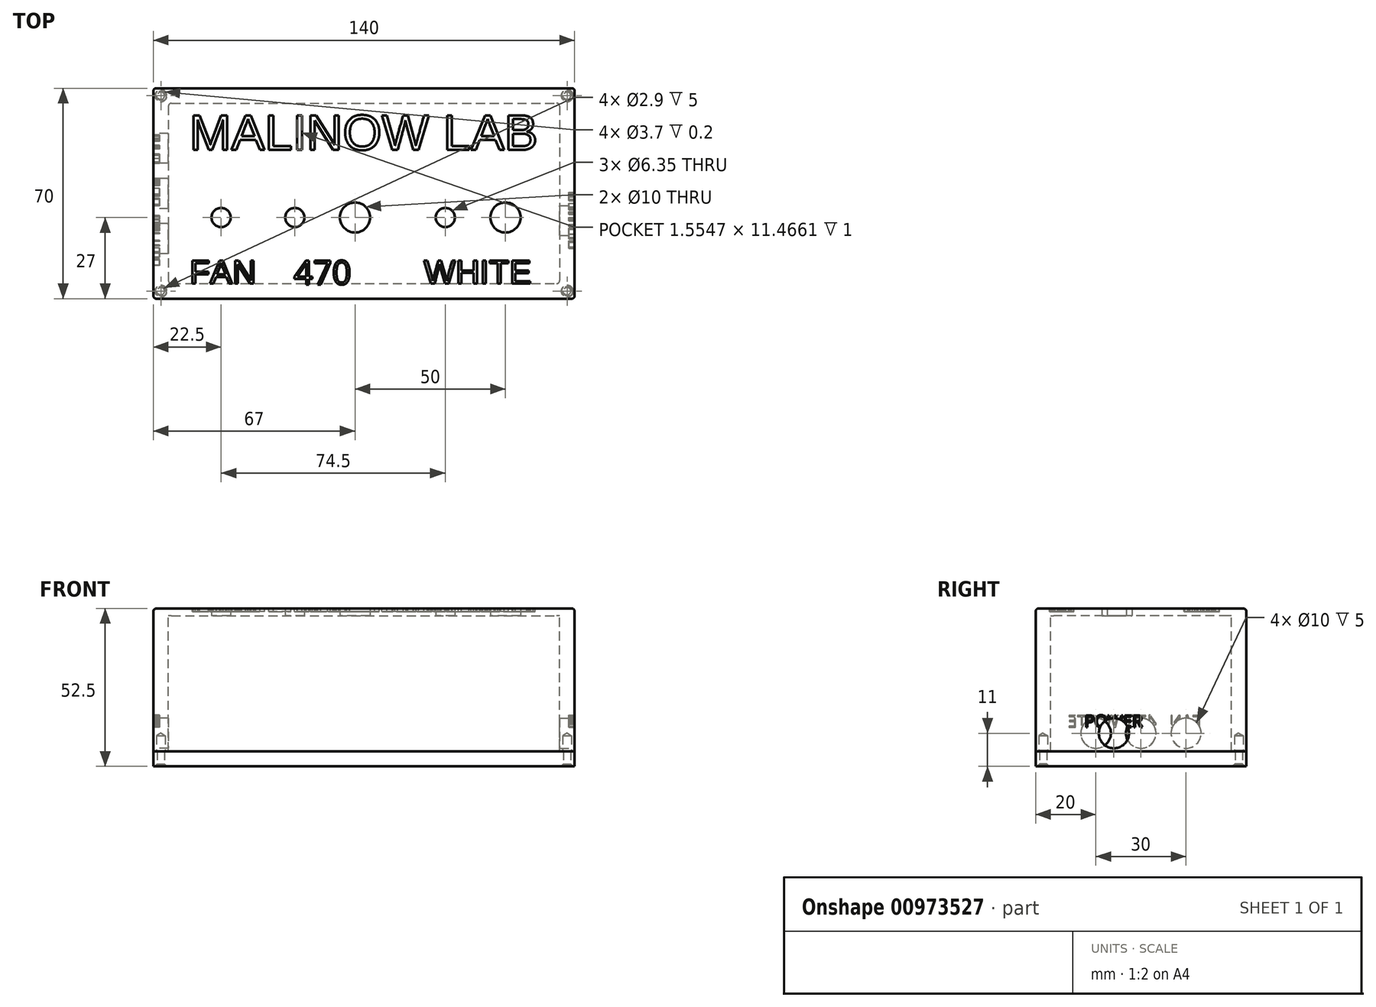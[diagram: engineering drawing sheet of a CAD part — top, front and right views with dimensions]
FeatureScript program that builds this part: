
annotation { "Feature Type Name" : "Feature", "Feature Type Description" : "" }
export const myFeature = defineFeature(function(context is Context, id is Id, definition is map)
    precondition{}
    {
        {
            var Q0;
            Q0=qCreatedBy(makeId("Top.planeOp"),FACE);
            var sketch = newSketch(context, id + "F0", { "sketchPlane" : qUnion([Q0])});
            skLineSegment(sketch, "E0.bottom", {"start": v(0, 0) * mm, "end": v(140, 0) * mm});
            skLineSegment(sketch, "E0.top", {"start": v(0, 70) * mm, "end": v(140, 70) * mm});
            skLineSegment(sketch, "E0.left", {"start": v(0, 0) * mm, "end": v(0, 70) * mm});
            skLineSegment(sketch, "E0.right", {"start": v(140, 0) * mm, "end": v(140, 70) * mm});
            skCircle(sketch, "E1", {"center": v(117, 27) * mm, "radius": 5 * mm});
            skCircle(sketch, "E2", {"center": v(67, 27) * mm, "radius": 5 * mm});
            skCircle(sketch, "E3", {"center": v(22.5, 27) * mm, "radius": 3.18 * mm});
            skLineSegment(sketch, "E4", {"start": v(5, 70) * mm, "end": v(5, 5) * mm, "construction": true});
            skLineSegment(sketch, "E5", {"start": v(5, 5) * mm, "end": v(135, 5) * mm, "construction": true});
            skLineSegment(sketch, "E6", {"start": v(135, 5) * mm, "end": v(135, 70) * mm, "construction": true});
            skLineSegment(sketch, "E7", {"start": v(0, 65) * mm, "end": v(140, 65) * mm, "construction": true});
            skLineSegment(sketch, "E8", {"start": v(5, 5) * mm, "end": v(0, 5) * mm, "construction": true});
            skLineSegment(sketch, "E9", {"start": v(135, 5) * mm, "end": v(140, 5) * mm, "construction": true});
            skPoint(sketch, "E10.endSnap0", {"position": v(5, 37.5) * mm});
            skLineSegment(sketch, "E11", {"start": v(5, 70) * mm, "end": v(135, 65) * mm, "construction": true});
            skLineSegment(sketch, "E12", {"start": v(135, 70) * mm, "end": v(5, 65) * mm, "construction": true});
            skLineSegment(sketch, "E13", {"start": v(140, 5) * mm, "end": v(0, 0) * mm, "construction": true});
            skLineSegment(sketch, "E14", {"start": v(0, 5) * mm, "end": v(140, 0) * mm, "construction": true});
            skPoint(sketch, "E15", {"position": v(70, 2.5) * mm});
            skPoint(sketch, "E16", {"position": v(70, 67.5) * mm});
            skLineSegment(sketch, "E17", {"start": v(5, 27) * mm, "end": v(135, 27) * mm, "construction": true});
            skCircle(sketch, "E18", {"center": v(47, 27) * mm, "radius": 3.18 * mm});
            skCircle(sketch, "E19", {"center": v(97, 27) * mm, "radius": 3.18 * mm});
            skSolve(sketch);
        }
        {
            var Q0;
            Q0=makeQuery(id+"F0.imprint","IMPRINT",FACE,{"disambiguationData":[TD([[makeQuery(id+"F0.imprint","IMPRINT",EDGE,{"derivedFrom":sQuery(id+"F0.wireOp",EDGE,"E0.bottom")}),1.0]])]});
            extrude(context, id + "F1", {"entities" : qUnion([Q0]), "depth" : 2.5 * mm, "offsetDistance" : 25 * mm});
        }
        {
            var Q0;
            Q0=makeQuery(id+"F1.opExtrude","CAP_FACE",FACE,{"disambiguationData":[OSD([sQuery(id+"F0.wireOp",EDGE,"E0.bottom"),sQuery(id+"F0.wireOp",EDGE,"E0.top"),sQuery(id+"F0.wireOp",EDGE,"E0.left"),sQuery(id+"F0.wireOp",EDGE,"E0.right"),sQuery(id+"F0.wireOp",EDGE,"E1"),sQuery(id+"F0.wireOp",EDGE,"E2"),sQuery(id+"F0.wireOp",EDGE,"E3")])],"isStart":true});
            var sketch = newSketch(context, id + "F2", { "sketchPlane" : qUnion([Q0])});
            skLineSegment(sketch, "E20.bottom", {"start": v(0, -70) * mm, "end": v(140, -70) * mm, "construction": true});
            skLineSegment(sketch, "E20.top", {"start": v(0, 0) * mm, "end": v(140, 0) * mm, "construction": true});
            skLineSegment(sketch, "E20.left", {"start": v(0, -70) * mm, "end": v(0, 0) * mm, "construction": true});
            skLineSegment(sketch, "E20.right", {"start": v(140, -70) * mm, "end": v(140, 0) * mm, "construction": true});
            skLineSegment(sketch, "E21.bottom", {"start": v(5, -65) * mm, "end": v(135, -65) * mm});
            skLineSegment(sketch, "E21.top", {"start": v(5, -5) * mm, "end": v(135, -5) * mm});
            skLineSegment(sketch, "E21.left", {"start": v(5, -65) * mm, "end": v(5, -5) * mm});
            skLineSegment(sketch, "E21.right", {"start": v(135, -65) * mm, "end": v(135, -5) * mm});
            skSolve(sketch);
        }
        {
            var Q0;
            Q0=makeQuery(id+"F2.imprint","IMPRINT",FACE,{"disambiguationData":[TD([[makeQuery(id+"F2.imprint","IMPRINT",EDGE,{"derivedFrom":sQuery(id+"F2.wireOp",EDGE,"E21.bottom")}),-1.0]])]});
            var Q1;
            Q1=makeQuery(id+"F2.imprint","IMPRINT",FACE,{"disambiguationData":[TD([[makeQuery(id+"F2.imprint","IMPRINT",EDGE,{"derivedFrom":makeQuery(id+"FxvTJw6m9mzOm3c_1.hole-0.boolean.opBoolean","INTERSECT",EDGE,{"derivedFrom":[makeQuery(id+"F1.opExtrude","CAP_FACE",FACE,{"disambiguationData":[OSD([sQuery(id+"F0.wireOp",EDGE,"E0.bottom"),sQuery(id+"F0.wireOp",EDGE,"E0.top"),sQuery(id+"F0.wireOp",EDGE,"E0.left"),sQuery(id+"F0.wireOp",EDGE,"E0.right"),sQuery(id+"F0.wireOp",EDGE,"E1"),sQuery(id+"F0.wireOp",EDGE,"E2"),sQuery(id+"F0.wireOp",EDGE,"E3")])],"isStart":true}),makeQuery(id+"FxvTJw6m9mzOm3c_1.hole-0.opRevolve","SWEPT_FACE",FACE,{"disambiguationData":[OSD([sQuery(id+"FxvTJw6m9mzOm3c_1.hole-0.sketch.wireOp",EDGE,"core_line_2")])]})]})}),1.0]])]});
            var Q2;
            Q2=makeQuery(id+"F2.imprint","IMPRINT",FACE,{"disambiguationData":[TD([[makeQuery(id+"F2.imprint","IMPRINT",EDGE,{"derivedFrom":makeQuery(id+"FxvTJw6m9mzOm3c_1.hole-1.boolean.opBoolean","INTERSECT",EDGE,{"derivedFrom":[makeQuery(id+"F1.opExtrude","CAP_FACE",FACE,{"disambiguationData":[OSD([sQuery(id+"F0.wireOp",EDGE,"E0.bottom"),sQuery(id+"F0.wireOp",EDGE,"E0.top"),sQuery(id+"F0.wireOp",EDGE,"E0.left"),sQuery(id+"F0.wireOp",EDGE,"E0.right"),sQuery(id+"F0.wireOp",EDGE,"E1"),sQuery(id+"F0.wireOp",EDGE,"E2"),sQuery(id+"F0.wireOp",EDGE,"E3")])],"isStart":true}),makeQuery(id+"FxvTJw6m9mzOm3c_1.hole-1.opRevolve","SWEPT_FACE",FACE,{"disambiguationData":[OSD([sQuery(id+"FxvTJw6m9mzOm3c_1.hole-1.sketch.wireOp",EDGE,"core_line_2")])]})]})}),1.0]])]});
            var Q3;
            Q3=makeQuery(id+"F2.imprint","IMPRINT",FACE,{"disambiguationData":[TD([[makeQuery(id+"F2.imprint","IMPRINT",EDGE,{"derivedFrom":makeQuery(id+"FxvTJw6m9mzOm3c_1.hole-2.boolean.opBoolean","INTERSECT",EDGE,{"derivedFrom":[makeQuery(id+"F1.opExtrude","CAP_FACE",FACE,{"disambiguationData":[OSD([sQuery(id+"F0.wireOp",EDGE,"E0.bottom"),sQuery(id+"F0.wireOp",EDGE,"E0.top"),sQuery(id+"F0.wireOp",EDGE,"E0.left"),sQuery(id+"F0.wireOp",EDGE,"E0.right"),sQuery(id+"F0.wireOp",EDGE,"E1"),sQuery(id+"F0.wireOp",EDGE,"E2"),sQuery(id+"F0.wireOp",EDGE,"E3")])],"isStart":true}),makeQuery(id+"FxvTJw6m9mzOm3c_1.hole-2.opRevolve","SWEPT_FACE",FACE,{"disambiguationData":[OSD([sQuery(id+"FxvTJw6m9mzOm3c_1.hole-2.sketch.wireOp",EDGE,"core_line_2")])]})]})}),1.0]])]});
            var Q4;
            Q4=makeQuery(id+"F2.imprint","IMPRINT",FACE,{"disambiguationData":[TD([[makeQuery(id+"F2.imprint","IMPRINT",EDGE,{"derivedFrom":makeQuery(id+"FxvTJw6m9mzOm3c_1.hole-3.boolean.opBoolean","INTERSECT",EDGE,{"derivedFrom":[makeQuery(id+"F1.opExtrude","CAP_FACE",FACE,{"disambiguationData":[OSD([sQuery(id+"F0.wireOp",EDGE,"E0.bottom"),sQuery(id+"F0.wireOp",EDGE,"E0.top"),sQuery(id+"F0.wireOp",EDGE,"E0.left"),sQuery(id+"F0.wireOp",EDGE,"E0.right"),sQuery(id+"F0.wireOp",EDGE,"E1"),sQuery(id+"F0.wireOp",EDGE,"E2"),sQuery(id+"F0.wireOp",EDGE,"E3")])],"isStart":true}),makeQuery(id+"FxvTJw6m9mzOm3c_1.hole-3.opRevolve","SWEPT_FACE",FACE,{"disambiguationData":[OSD([sQuery(id+"FxvTJw6m9mzOm3c_1.hole-3.sketch.wireOp",EDGE,"core_line_2")])]})]})}),1.0]])]});
            extrude(context, id + "F3", {"entities" : qUnion([Q0, Q1, Q2, Q3, Q4]), "depth" : 45 * mm, "offsetDistance" : 25 * mm});
        }
        {
            var Q0;
            Q0=makeQuery(id+"F3.opExtrude","CAP_FACE",FACE,{"disambiguationData":[OSD([sQuery(id+"F0.wireOp",EDGE,"E0.bottom"),sQuery(id+"F0.wireOp",EDGE,"E0.top"),sQuery(id+"F0.wireOp",EDGE,"E0.left"),sQuery(id+"F0.wireOp",EDGE,"E0.right"),sQuery(id+"F2.wireOp",EDGE,"E21.bottom"),sQuery(id+"F2.wireOp",EDGE,"E21.top"),sQuery(id+"F2.wireOp",EDGE,"E21.left"),sQuery(id+"F2.wireOp",EDGE,"E21.right")])],"isStart":false});
            var sketch = newSketch(context, id + "F4", { "sketchPlane" : qUnion([Q0])});
            skLineSegment(sketch, "E22.bottom", {"start": v(0, 0) * mm, "end": v(140, 0) * mm});
            skLineSegment(sketch, "E22.top", {"start": v(0, -70) * mm, "end": v(140, -70) * mm});
            skLineSegment(sketch, "E22.left", {"start": v(0, 0) * mm, "end": v(0, -70) * mm});
            skLineSegment(sketch, "E22.right", {"start": v(140, 0) * mm, "end": v(140, -70) * mm});
            skLineSegment(sketch, "E23.bottom", {"start": v(5, -5) * mm, "end": v(135, -5) * mm, "construction": true});
            skLineSegment(sketch, "E23.top", {"start": v(5, -65) * mm, "end": v(135, -65) * mm, "construction": true});
            skLineSegment(sketch, "E23.left", {"start": v(5, -5) * mm, "end": v(5, -65) * mm, "construction": true});
            skLineSegment(sketch, "E23.right", {"start": v(135, -5) * mm, "end": v(135, -65) * mm, "construction": true});
            skSolve(sketch);
        }
        {
            var Q0;
            Q0=makeQuery(id+"F4.imprint","IMPRINT",FACE,{"disambiguationData":[TD([[makeQuery(id+"F4.imprint","IMPRINT",EDGE,{"derivedFrom":sQuery(id+"F4.wireOp",EDGE,"E22.bottom")}),-1.0]])]});
            var Q1;
            Q1=makeQuery(id+"F4.imprint","IMPRINT",FACE,{"disambiguationData":[TD([[makeQuery(id+"F4.imprint","IMPRINT",EDGE,{"derivedFrom":makeQuery(id+"F3.opExtrude","CAP_EDGE",EDGE,{"disambiguationData":[OSD([sQuery(id+"F2.wireOp",EDGE,"E21.bottom")])],"isStart":false})}),1.0]])]});
            extrude(context, id + "F5", {"entities" : qUnion([Q0, Q1]), "depth" : 5 * mm, "offsetDistance" : 25 * mm});
        }
        {
            var Q0;
            Q0=makeQuery(id+"F5.opExtrude","CAP_FACE",FACE,{"disambiguationData":[OSD([sQuery(id+"F4.wireOp",EDGE,"E22.bottom"),sQuery(id+"F4.wireOp",EDGE,"E22.top"),sQuery(id+"F4.wireOp",EDGE,"E22.left"),sQuery(id+"F4.wireOp",EDGE,"E22.right")])],"isStart":false});
            var sketch = newSketch(context, id + "F6", { "sketchPlane" : qUnion([Q0])});
            skLineSegment(sketch, "E24.bottom", {"start": v(0, -70) * mm, "end": v(140, -70) * mm, "construction": true});
            skLineSegment(sketch, "E24.top", {"start": v(0, 0) * mm, "end": v(140, 0) * mm, "construction": true});
            skLineSegment(sketch, "E24.left", {"start": v(0, -70) * mm, "end": v(0, 0) * mm, "construction": true});
            skLineSegment(sketch, "E24.right", {"start": v(140, -70) * mm, "end": v(140, 0) * mm, "construction": true});
            skLineSegment(sketch, "E25.bottom", {"start": v(5, -65) * mm, "end": v(135, -65) * mm, "construction": true});
            skLineSegment(sketch, "E25.top", {"start": v(5, -5) * mm, "end": v(135, -5) * mm, "construction": true});
            skLineSegment(sketch, "E25.left", {"start": v(5, -65) * mm, "end": v(5, -5) * mm, "construction": true});
            skLineSegment(sketch, "E25.right", {"start": v(135, -65) * mm, "end": v(135, -5) * mm, "construction": true});
            skLineSegment(sketch, "E26", {"start": v(5, -5) * mm, "end": v(0, 0) * mm, "construction": true});
            skLineSegment(sketch, "E27", {"start": v(135, -5) * mm, "end": v(140, 0) * mm, "construction": true});
            skLineSegment(sketch, "E28", {"start": v(135, -65) * mm, "end": v(140, -70) * mm, "construction": true});
            skLineSegment(sketch, "E29", {"start": v(5, -65) * mm, "end": v(0, -70) * mm, "construction": true});
            skPoint(sketch, "E30", {"position": v(2.5, -2.5) * mm});
            skPoint(sketch, "E31", {"position": v(137.5, -2.5) * mm});
            skPoint(sketch, "E32", {"position": v(137.5, -67.5) * mm});
            skPoint(sketch, "E33", {"position": v(2.5, -67.5) * mm});
            skSolve(sketch);
        }
        {
            var Q0;
            Q0=sQuery(id+"F6.wireOp",VERTEX,"E30");
            var Q1;
            Q1=sQuery(id+"F6.wireOp",VERTEX,"E33");
            var Q2;
            Q2=sQuery(id+"F6.wireOp",VERTEX,"E32");
            var Q3;
            Q3=sQuery(id+"F6.wireOp",VERTEX,"E31");
            var Q4;
            Q4=makeQuery(id+"F3.opExtrude","SWEPT_BODY",BODY,{"disambiguationData":[OSD([sQuery(id+"F0.wireOp",EDGE,"E0.bottom"),sQuery(id+"F0.wireOp",EDGE,"E0.top"),sQuery(id+"F0.wireOp",EDGE,"E0.left"),sQuery(id+"F0.wireOp",EDGE,"E0.right"),sQuery(id+"F2.wireOp",EDGE,"E21.bottom"),sQuery(id+"F2.wireOp",EDGE,"E21.top"),sQuery(id+"F2.wireOp",EDGE,"E21.left"),sQuery(id+"F2.wireOp",EDGE,"E21.right")])]});
            var Q5;
            Q5=makeQuery(id+"F5.opExtrude","SWEPT_BODY",BODY,{"disambiguationData":[OSD([sQuery(id+"F4.wireOp",EDGE,"E22.bottom"),sQuery(id+"F4.wireOp",EDGE,"E22.top"),sQuery(id+"F4.wireOp",EDGE,"E22.left"),sQuery(id+"F4.wireOp",EDGE,"E22.right")])]});
            hole(context, id + "F7", {"style" : HoleStyle.C_SINK, "endStyle" : HoleEndStyle.BLIND, "holeDiameter" : 2.4 * mm, "cSinkDiameter" : 4 * mm, "cSinkAngle" : 90 * degree, "majorDiameter" : 5 * mm, "holeDepth" : 5 * mm, "isTappedThrough" : true, "tappedDepth" : 12 * mm, "tapClearance" : 3, "locations" : qUnion([Q0, Q1, Q2, Q3]), "scope" : qUnion([Q4, Q5])});
        }
        {
            var Q0;
            Q0=makeQuery(id+"F3.opExtrude","CAP_FACE",FACE,{"disambiguationData":[OSD([sQuery(id+"F0.wireOp",EDGE,"E0.bottom"),sQuery(id+"F0.wireOp",EDGE,"E0.top"),sQuery(id+"F0.wireOp",EDGE,"E0.left"),sQuery(id+"F0.wireOp",EDGE,"E0.right"),sQuery(id+"F2.wireOp",EDGE,"E21.bottom"),sQuery(id+"F2.wireOp",EDGE,"E21.top"),sQuery(id+"F2.wireOp",EDGE,"E21.left"),sQuery(id+"F2.wireOp",EDGE,"E21.right")])],"isStart":false});
            var sketch = newSketch(context, id + "F8", { "sketchPlane" : qUnion([Q0])});
            skPoint(sketch, "E34", {"position": v(2.5, -2.5) * mm});
            skPoint(sketch, "E35", {"position": v(2.5, -67.5) * mm});
            skPoint(sketch, "E36", {"position": v(137.5, -67.5) * mm});
            skPoint(sketch, "E37", {"position": v(137.5, -2.5) * mm});
            skSolve(sketch);
        }
        {
            var Q0;
            Q0=sQuery(id+"F8.wireOp",VERTEX,"E34");
            var Q1;
            Q1=sQuery(id+"F8.wireOp",VERTEX,"E35");
            var Q2;
            Q2=sQuery(id+"F8.wireOp",VERTEX,"E36");
            var Q3;
            Q3=sQuery(id+"F8.wireOp",VERTEX,"E37");
            var Q4;
            Q4=makeQuery(id+"F3.opExtrude","SWEPT_BODY",BODY,{"disambiguationData":[OSD([sQuery(id+"F0.wireOp",EDGE,"E0.bottom"),sQuery(id+"F0.wireOp",EDGE,"E0.top"),sQuery(id+"F0.wireOp",EDGE,"E0.left"),sQuery(id+"F0.wireOp",EDGE,"E0.right"),sQuery(id+"F2.wireOp",EDGE,"E21.bottom"),sQuery(id+"F2.wireOp",EDGE,"E21.top"),sQuery(id+"F2.wireOp",EDGE,"E21.left"),sQuery(id+"F2.wireOp",EDGE,"E21.right")])]});
            hole(context, id + "F9", {"style" : HoleStyle.C_BORE, "endStyle" : HoleEndStyle.BLIND, "holeDiameter" : 2.9 * mm, "cBoreDiameter" : 3.7 * mm, "cBoreDepth" : .2 * mm, "majorDiameter" : 5 * mm, "holeDepth" : 5.2 * mm, "isTappedThrough" : true, "tappedDepth" : 12 * mm, "tapClearance" : 3, "locations" : qUnion([Q0, Q1, Q2, Q3]), "scope" : qUnion([Q4])});
        }
        {
            var Q0;
            Q0=makeQuery(id+"F1.opExtrude","CAP_EDGE",EDGE,{"disambiguationData":[OSD([sQuery(id+"F0.wireOp",EDGE,"E0.bottom")])],"isStart":false});
            var Q1;
            Q1=makeQuery(id+"F1.opExtrude","CAP_EDGE",EDGE,{"disambiguationData":[OSD([sQuery(id+"F0.wireOp",EDGE,"E0.left")])],"isStart":false});
            var Q2;
            Q2=makeQuery(id+"F1.opExtrude","CAP_EDGE",EDGE,{"disambiguationData":[OSD([sQuery(id+"F0.wireOp",EDGE,"E0.top")])],"isStart":false});
            var Q3;
            Q3=makeQuery(id+"F1.opExtrude","CAP_EDGE",EDGE,{"disambiguationData":[OSD([sQuery(id+"F0.wireOp",EDGE,"E0.right")])],"isStart":false});
            var Q4;
            Q4=makeQuery(id+"F3.opExtrude","SWEPT_EDGE",EDGE,{"disambiguationData":[OSD([sQuery(id+"F0.wireOp",EDGE,"E0.bottom"),sQuery(id+"F0.wireOp",EDGE,"E0.right")])]});
            var Q5;
            Q5=makeQuery(id+"F3.opExtrude","SWEPT_EDGE",EDGE,{"disambiguationData":[OSD([sQuery(id+"F0.wireOp",EDGE,"E0.bottom"),sQuery(id+"F0.wireOp",EDGE,"E0.left")])]});
            var Q6;
            Q6=makeQuery(id+"F1.opExtrude","SWEPT_EDGE",EDGE,{"disambiguationData":[OSD([sQuery(id+"F0.wireOp",EDGE,"E0.bottom"),sQuery(id+"F0.wireOp",EDGE,"E0.left")])]});
            var Q7;
            Q7=makeQuery(id+"F1.opExtrude","SWEPT_EDGE",EDGE,{"disambiguationData":[OSD([sQuery(id+"F0.wireOp",EDGE,"E0.bottom"),sQuery(id+"F0.wireOp",EDGE,"E0.right")])]});
            var Q8;
            Q8=makeQuery(id+"F3.opExtrude","SWEPT_EDGE",EDGE,{"disambiguationData":[OSD([sQuery(id+"F0.wireOp",EDGE,"E0.top"),sQuery(id+"F0.wireOp",EDGE,"E0.right")])]});
            var Q9;
            Q9=makeQuery(id+"F1.opExtrude","SWEPT_EDGE",EDGE,{"disambiguationData":[OSD([sQuery(id+"F0.wireOp",EDGE,"E0.top"),sQuery(id+"F0.wireOp",EDGE,"E0.right")])]});
            var Q10;
            Q10=makeQuery(id+"F3.opExtrude","SWEPT_EDGE",EDGE,{"disambiguationData":[OSD([sQuery(id+"F0.wireOp",EDGE,"E0.top"),sQuery(id+"F0.wireOp",EDGE,"E0.left")])]});
            var Q11;
            Q11=makeQuery(id+"F1.opExtrude","SWEPT_EDGE",EDGE,{"disambiguationData":[OSD([sQuery(id+"F0.wireOp",EDGE,"E0.top"),sQuery(id+"F0.wireOp",EDGE,"E0.left")])]});
            var Q12;
            Q12=makeQuery(id+"F5.opExtrude","SWEPT_EDGE",EDGE,{"disambiguationData":[OSD([sQuery(id+"F4.wireOp",EDGE,"E22.top"),sQuery(id+"F4.wireOp",EDGE,"E22.left")])]});
            var Q13;
            Q13=makeQuery(id+"F5.opExtrude","SWEPT_EDGE",EDGE,{"disambiguationData":[OSD([sQuery(id+"F4.wireOp",EDGE,"E22.bottom"),sQuery(id+"F4.wireOp",EDGE,"E22.left")])]});
            var Q14;
            Q14=makeQuery(id+"F5.opExtrude","SWEPT_EDGE",EDGE,{"disambiguationData":[OSD([sQuery(id+"F4.wireOp",EDGE,"E22.top"),sQuery(id+"F4.wireOp",EDGE,"E22.right")])]});
            var Q15;
            Q15=makeQuery(id+"F5.opExtrude","SWEPT_EDGE",EDGE,{"disambiguationData":[OSD([sQuery(id+"F4.wireOp",EDGE,"E22.bottom"),sQuery(id+"F4.wireOp",EDGE,"E22.right")])]});
            fillet(context, id + "F10", {"entities" : qUnion([Q0, Q1, Q2, Q3, Q4, Q5, Q6, Q7, Q8, Q9, Q10, Q11, Q12, Q13, Q14, Q15]), "radius" : 1 * mm, "tangentPropagation" : true, "allowEdgeOverflow" : false});
        }
        {
            var Q0;
            Q0=makeQuery(id+"F3.opExtrude","SWEPT_FACE",FACE,{"disambiguationData":[OSD([sQuery(id+"F0.wireOp",EDGE,"E0.left")])]});
            var sketch = newSketch(context, id + "F11", { "sketchPlane" : qUnion([Q0])});
            skCircle(sketch, "E38", {"center": v(-20, -39) * mm, "radius": 5 * mm});
            skLineSegment(sketch, "E39", {"start": v(-35, -45) * mm, "end": v(-35, 0) * mm, "construction": true});
            skLineSegment(sketch, "E40", {"start": v(-20, -39) * mm, "end": v(-70.23, -39) * mm, "construction": true});
            skCircle(sketch, "E41", {"center": v(-35, -39) * mm, "radius": 5 * mm});
            skCircle(sketch, "E42", {"center": v(-50, -39) * mm, "radius": 5 * mm});
            skSolve(sketch);
        }
        {
            var Q0;
            Q0=makeQuery(id+"F3.opExtrude","SWEPT_FACE",FACE,{"disambiguationData":[OSD([sQuery(id+"F0.wireOp",EDGE,"E0.right")])]});
            var sketch = newSketch(context, id + "F12", { "sketchPlane" : qUnion([Q0])});
            skLineSegment(sketch, "E43", {"start": v(1, -39) * mm, "end": v(69, -39) * mm, "construction": true});
            skCircle(sketch, "E44", {"center": v(26, -39) * mm, "radius": 5 * mm});
            skCircle(sketch, "E45", {"center": v(40, -39) * mm, "radius": 5 * mm});
            skCircle(sketch, "E46", {"center": v(54, -39) * mm, "radius": 5 * mm});
            skSolve(sketch);
        }
        {
            var Q0;
            Q0=makeQuery(id+"F10.opFillet","SPLIT",FACE,{"disambiguationData":[OD(4.0)],"derivedFrom":makeQuery(id+"F1.opExtrude","CAP_FACE",FACE,{"disambiguationData":[OSD([sQuery(id+"F0.wireOp",EDGE,"E0.bottom"),sQuery(id+"F0.wireOp",EDGE,"E0.top"),sQuery(id+"F0.wireOp",EDGE,"E0.left"),sQuery(id+"F0.wireOp",EDGE,"E0.right"),sQuery(id+"F0.wireOp",EDGE,"E1"),sQuery(id+"F0.wireOp",EDGE,"E2"),sQuery(id+"F0.wireOp",EDGE,"E3")])],"isStart":false})});
            var sketch = newSketch(context, id + "F13", { "sketchPlane" : qUnion([Q0])});
            skLineSegment(sketch, "E47.bottom", {"start": v(1, 61.5) * mm, "end": v(139, 61.5) * mm, "construction": true});
            skLineSegment(sketch, "E47.top", {"start": v(1, 49.5) * mm, "end": v(139, 49.5) * mm, "construction": true});
            skLineSegment(sketch, "E47.left", {"start": v(1, 61.5) * mm, "end": v(1, 49.5) * mm, "construction": true});
            skLineSegment(sketch, "E47.right", {"start": v(139, 61.5) * mm, "end": v(139, 49.5) * mm, "construction": true});
            skLineSegment(sketch, "E48", {"start": v(70, 61.5) * mm, "end": v(70, 49.5) * mm, "construction": true});
            skLineSegment(sketch, "E49.bottom", {"start": v(100.24, 61.5) * mm, "end": v(11.98, 61.5) * mm, "construction": true});
            skLineSegment(sketch, "E49.top", {"start": v(128.02, 49.5) * mm, "end": v(39.76, 49.5) * mm, "construction": true});
            skLineSegment(sketch, "E49.left", {"start": v(100.24, 61.5) * mm, "end": v(128.02, 49.5) * mm, "construction": true});
            skLineSegment(sketch, "E49.right", {"start": v(11.98, 61.5) * mm, "end": v(39.76, 49.5) * mm, "construction": true});
            skPoint(sketch, "E49.middle", {"position": v(70, 55.5) * mm});
            skText(sketch, "E50", { "text": "MALINOW LAB", "fontName": "Arimo-Regular.ttf"});
            const initialGuessF13  = {"E50": [0.01198, 0.0495, 1, 0, 0.012]};
            skSetInitialGuess(sketch, initialGuessF13);
            skSolve(sketch);
        }
        {
            var Q0;
            Q0=qSketchRegion(id+"F13",true);
            extrude(context, id + "F14", {"entities" : qUnion([Q0]), "operationType" : NewBodyOperationType.REMOVE, "oppositeDirection" : true, "depth" : 1 * mm, "offsetDistance" : 25 * mm});
        }
        {
            var Q0;
            Q0=makeQuery(id+"F3.opExtrude","SWEPT_BODY",BODY,{"disambiguationData":[OSD([sQuery(id+"F0.wireOp",EDGE,"E0.bottom"),sQuery(id+"F0.wireOp",EDGE,"E0.top"),sQuery(id+"F0.wireOp",EDGE,"E0.left"),sQuery(id+"F0.wireOp",EDGE,"E0.right"),sQuery(id+"F2.wireOp",EDGE,"E21.bottom"),sQuery(id+"F2.wireOp",EDGE,"E21.top"),sQuery(id+"F2.wireOp",EDGE,"E21.left"),sQuery(id+"F2.wireOp",EDGE,"E21.right")])]});
            var Q1;
            Q1=makeQuery(id+"F1.opExtrude","SWEPT_BODY",BODY,{"disambiguationData":[OSD([sQuery(id+"F0.wireOp",EDGE,"E0.bottom"),sQuery(id+"F0.wireOp",EDGE,"E0.top"),sQuery(id+"F0.wireOp",EDGE,"E0.left"),sQuery(id+"F0.wireOp",EDGE,"E0.right"),sQuery(id+"F0.wireOp",EDGE,"E1"),sQuery(id+"F0.wireOp",EDGE,"E2"),sQuery(id+"F0.wireOp",EDGE,"E3")])]});
            booleanBodies(context, id + "F15", {"operationType" : BooleanOperationType.UNION, "tools" : qUnion([Q0, Q1])});
        }
        {
            var Q0;
            {var subQ0=sQuery(id+"F0.wireOp",EDGE,"E0.right");var subQ1=sQuery(id+"F0.wireOp",EDGE,"E0.left");var subQ2=sQuery(id+"F0.wireOp",EDGE,"E0.top");var subQ3=sQuery(id+"F0.wireOp",EDGE,"E0.bottom");var subQ4=sQuery(id+"F0.wireOp",EDGE,"E3");var subQ5=sQuery(id+"F0.wireOp",EDGE,"E2");var subQ6=sQuery(id+"F0.wireOp",EDGE,"E1");Q0=makeQuery(id+"F14.boolean.opBoolean","SPLIT",FACE,{"disambiguationData":[TD([makeQuery(id+"F1.opExtrude","SWEPT_FACE",FACE,{"disambiguationData":[OSD([subQ6])]})])],"derivedFrom":makeQuery(id+"F1.opExtrude","CAP_FACE",FACE,{"disambiguationData":[OSD([subQ3,subQ2,subQ1,subQ0,subQ6,subQ5,subQ4])],"isStart":false})});}
            var sketch = newSketch(context, id + "F16", { "sketchPlane" : qUnion([Q0])});
            skText(sketch, "E51", { "text": "FAN", "fontName": "Arimo-Regular.ttf"});
            skText(sketch, "E52", { "text": "WHITE", "fontName": "Arimo-Regular.ttf"});
            skText(sketch, "E53", { "text": "470\n", "fontName": "OpenSans-Regular.ttf"});
            const initialGuessF16  = {"E51": [0.012, 0.005, 1, 0, 0.008], "E52": [0.0899, 0.005, 1, 0, 0.008], "E53": [0.04668, 0.00472, 1, 0, 0.008]};
            skSetInitialGuess(sketch, initialGuessF16);
            skSolve(sketch);
        }
        {
            var Q0;
            Q0=qSketchRegion(id+"F16",true);
            extrude(context, id + "F17", {"entities" : qUnion([Q0]), "operationType" : NewBodyOperationType.REMOVE, "oppositeDirection" : true, "depth" : 1 * mm, "offsetDistance" : 25 * mm});
        }
        {
            var Q0;
            Q0=makeQuery(id+"F5.opExtrude","CAP_FACE",FACE,{"disambiguationData":[OSD([sQuery(id+"F4.wireOp",EDGE,"E22.bottom"),sQuery(id+"F4.wireOp",EDGE,"E22.top"),sQuery(id+"F4.wireOp",EDGE,"E22.left"),sQuery(id+"F4.wireOp",EDGE,"E22.right")])],"isStart":true});
            var sketch = newSketch(context, id + "F18", { "sketchPlane" : qUnion([Q0])});
            skLineSegment(sketch, "E54", {"start": v(70, 70) * mm, "end": v(70, 0) * mm, "construction": true});
            skLineSegment(sketch, "E55", {"start": v(140, 35) * mm, "end": v(0, 35) * mm, "construction": true});
            skPoint(sketch, "E56", {"position": v(50, 35) * mm});
            skPoint(sketch, "E57", {"position": v(90, 35) * mm});
            skSolve(sketch);
        }
        {
            var Q0;
            Q0 = qSketchRegion(id + "F11", true);
            extrude(context, id + "F19", {"entities" : qUnion([Q0]), "operationType" : NewBodyOperationType.REMOVE, "oppositeDirection" : true, "depth" : 25 * mm, "offsetDistance" : 25 * mm});
        }
        {
            var Q0;
            Q0=makeQuery(id+"F12.imprint","IMPRINT",FACE,{"disambiguationData":[TD([[makeQuery(id+"F12.imprint","IMPRINT",EDGE,{"derivedFrom":sQuery(id+"F12.wireOp",EDGE,"E44")}),1.0]])]});
            extrude(context, id + "F20", {"entities" : qUnion([Q0]), "operationType" : NewBodyOperationType.REMOVE, "oppositeDirection" : true, "depth" : 25 * mm, "offsetDistance" : 25 * mm});
        }
        {
            var Q0;
            {var subQ0=sQuery(id+"F0.wireOp",EDGE,"E0.left");Q0=makeQuery(id+"F15.opBoolean","MERGE",FACE,{"derivedFrom":[makeQuery(id+"F1.opExtrude","SWEPT_FACE",FACE,{"disambiguationData":[OSD([subQ0])]}),makeQuery(id+"F3.opExtrude","SWEPT_FACE",FACE,{"disambiguationData":[OSD([subQ0])]})]});}
            var sketch = newSketch(context, id + "F21", { "sketchPlane" : qUnion([Q0])});
            skText(sketch, "E58", { "text": "FAN   470  WHITE", "fontName": "OpenSans-Regular.ttf"});
            const initialGuessF21  = {"E58": [-0.055, -0.037, 1, 0, 0.004]};
            skSetInitialGuess(sketch, initialGuessF21);
            skSolve(sketch);
        }
        {
            var Q0;
            Q0 = qSketchRegion(id + "F21", true);
            extrude(context, id + "F22", {"entities" : qUnion([Q0]), "operationType" : NewBodyOperationType.REMOVE, "oppositeDirection" : true, "depth" : 2 * mm, "offsetDistance" : 25 * mm});
        }
        {
            var Q0;
            {var subQ0=sQuery(id+"F0.wireOp",EDGE,"E0.right");Q0=makeQuery(id+"F15.opBoolean","MERGE",FACE,{"derivedFrom":[makeQuery(id+"F1.opExtrude","SWEPT_FACE",FACE,{"disambiguationData":[OSD([subQ0])]}),makeQuery(id+"F3.opExtrude","SWEPT_FACE",FACE,{"disambiguationData":[OSD([subQ0])]})]});}
            var sketch = newSketch(context, id + "F23", { "sketchPlane" : qUnion([Q0])});
            skLineSegment(sketch, "E59", {"start": v(26, -39) * mm, "end": v(26, -35.17) * mm, "construction": true});
            skText(sketch, "E60", { "text": "POWER\n", "fontName": "OpenSans-Regular.ttf"});
            const initialGuessF23  = {"E60": [0.0162, -0.037, 1, 0, 0.004]};
            skSetInitialGuess(sketch, initialGuessF23);
            skSolve(sketch);
        }
        {
            var Q0;
            Q0 = qSketchRegion(id + "F23", true);
            extrude(context, id + "F24", {"entities" : qUnion([Q0]), "operationType" : NewBodyOperationType.REMOVE, "oppositeDirection" : true, "depth" : 2 * mm, "offsetDistance" : 25 * mm});
        }
        {
            var Q0;
            Q0=makeQuery(id+"F3.opExtrude","SWEPT_EDGE",EDGE,{"disambiguationData":[OSD([sQuery(id+"F2.wireOp",EDGE,"E21.top"),sQuery(id+"F2.wireOp",EDGE,"E21.left")])]});
            var Q1;
            Q1=makeQuery(id+"F3.opExtrude","SWEPT_EDGE",EDGE,{"disambiguationData":[OSD([sQuery(id+"F2.wireOp",EDGE,"E21.top"),sQuery(id+"F2.wireOp",EDGE,"E21.right")])]});
            var Q2;
            Q2=makeQuery(id+"F3.opExtrude","SWEPT_EDGE",EDGE,{"disambiguationData":[OSD([sQuery(id+"F2.wireOp",EDGE,"E21.bottom"),sQuery(id+"F2.wireOp",EDGE,"E21.right")])]});
            var Q3;
            Q3=makeQuery(id+"F3.opExtrude","SWEPT_EDGE",EDGE,{"disambiguationData":[OSD([sQuery(id+"F2.wireOp",EDGE,"E21.bottom"),sQuery(id+"F2.wireOp",EDGE,"E21.left")])]});
            fillet(context, id + "F25", {"entities" : qUnion([Q0, Q1, Q2, Q3]), "radius" : 1 * mm, "tangentPropagation" : true, "allowEdgeOverflow" : false});
        }
    });
